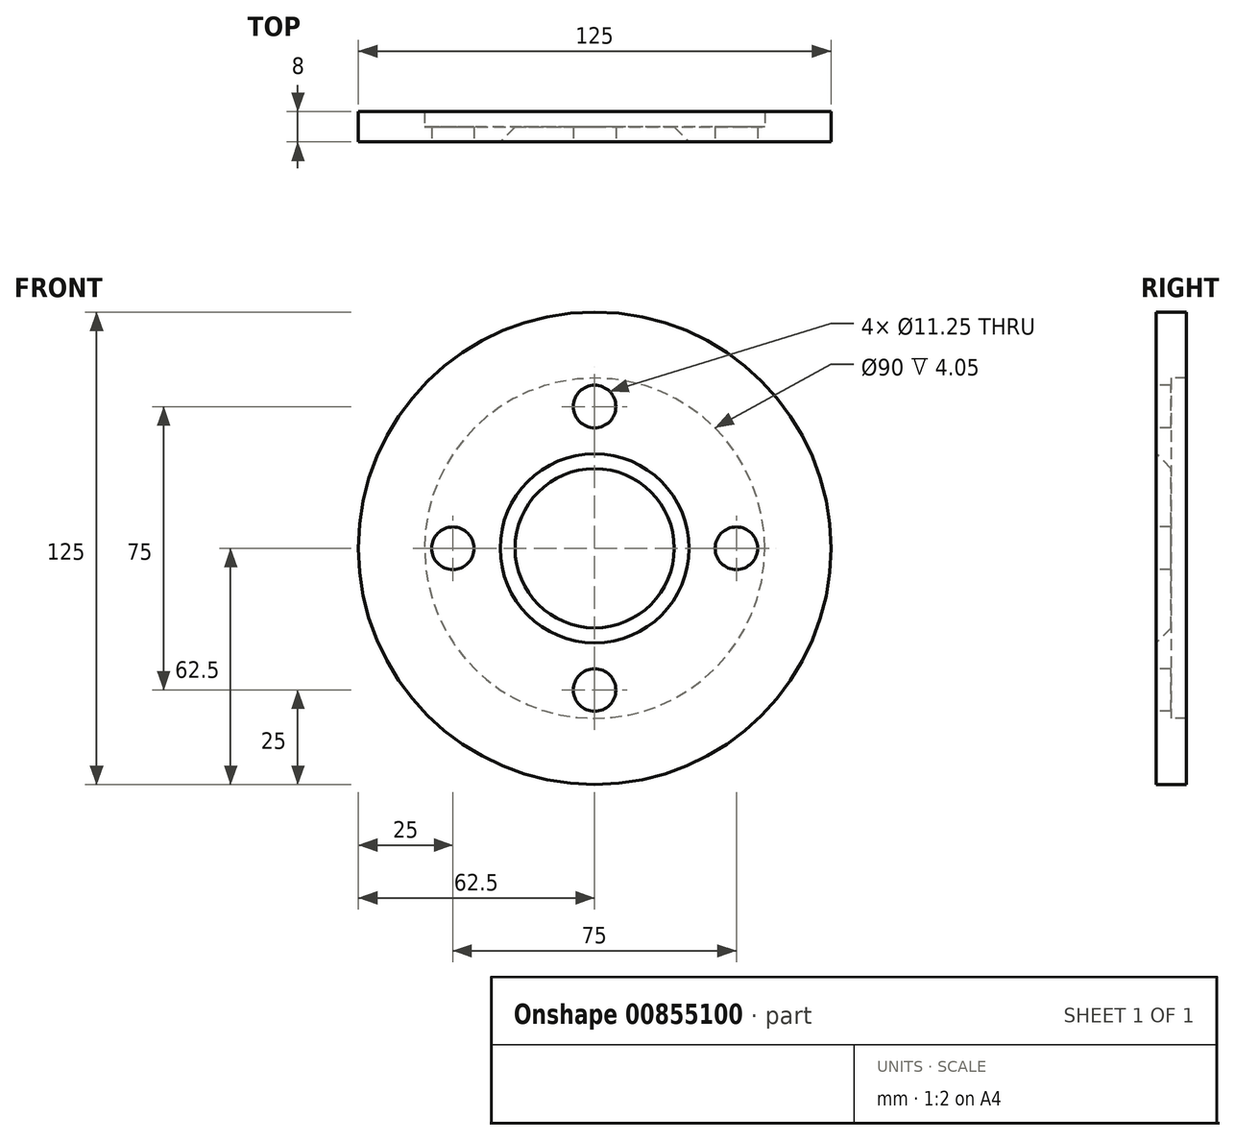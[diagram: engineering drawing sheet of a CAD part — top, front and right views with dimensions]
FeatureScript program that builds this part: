
annotation { "Feature Type Name" : "Feature", "Feature Type Description" : "" }
export const myFeature = defineFeature(function(context is Context, id is Id, definition is map)
    precondition{}
    {
        {
            var Q0;
            Q0=qCreatedBy(makeId("Front.planeOp"),FACE);
            var sketch = newSketch(context, id + "F0", { "sketchPlane" : qUnion([Q0])});
            skCircle(sketch, "E0", {"center": v(0, 0) * mm, "radius": 62.5 * mm});
            skCircle(sketch, "E1", {"center": v(0, 0) * mm, "radius": 37.5 * mm, "construction": true});
            skPoint(sketch, "E2", {"position": v(0, 37.5) * mm});
            skPoint(sketch, "E3", {"position": v(37.5, 0) * mm});
            skPoint(sketch, "E4.MirrorP", {"position": v(0, -37.5) * mm});
            skPoint(sketch, "E5.MirrorP", {"position": v(-37.5, 0) * mm});
            skCircle(sketch, "E6", {"center": v(0, 0) * mm, "radius": 45 * mm, "construction": true});
            skSolve(sketch);
        }
        {
            var Q0;
            Q0=makeQuery(id+"F0.imprint","IMPRINT",FACE,{"disambiguationData":[TD([[makeQuery(id+"F0.imprint","IMPRINT",EDGE,{"derivedFrom":sQuery(id+"F0.wireOp",EDGE,"E0")}),1.0]])]});
            extrude(context, id + "F1", {"entities" : qUnion([Q0]), "oppositeDirection" : true, "depth" : 3.95 * mm, "offsetDistance" : 25 * mm});
        }
        {
            var Q0;
            Q0=makeQuery(id+"F1.opExtrude","CAP_FACE",FACE,{"disambiguationData":[OSD([sQuery(id+"F0.wireOp",EDGE,"E0")])],"isStart":false});
            var sketch = newSketch(context, id + "F2", { "sketchPlane" : qUnion([Q0])});
            skCircle(sketch, "E7.0", {"center": v(0, 0) * mm, "radius": 45 * mm});
            skSolve(sketch);
        }
        {
            var Q0;
            Q0=makeQuery(id+"F2.imprint","IMPRINT",FACE,{"disambiguationData":[TD([[makeQuery(id+"F2.imprint","IMPRINT",EDGE,{"derivedFrom":sQuery(id+"F2.wireOp",EDGE,"E7.0")}),-1.0]])]});
            extrude(context, id + "F3", {"entities" : qUnion([Q0]), "operationType" : NewBodyOperationType.ADD, "depth" : 4.05 * mm, "offsetDistance" : 25 * mm});
        }
        {
            var Q0;
            Q0=qCreatedBy(makeId("Top.planeOp"),FACE);
            var sketch = newSketch(context, id + "F4", { "sketchPlane" : qUnion([Q0])});
            skLineSegment(sketch, "E8", {"start": v(0, 0) * mm, "end": v(0, 8) * mm});
            skLineSegment(sketch, "E9", {"start": v(0, 8) * mm, "end": v(18, 8) * mm});
            skLineSegment(sketch, "E10", {"start": v(18, 8) * mm, "end": v(18, 7) * mm});
            skLineSegment(sketch, "E11", {"start": v(18, 7) * mm, "end": v(25, 0) * mm});
            skLineSegment(sketch, "E12", {"start": v(25, 0) * mm, "end": v(0, 0) * mm});
            skSolve(sketch);
        }
        {
            var Q0;
            Q0=makeQuery(id+"F4.imprint","IMPRINT",FACE,{"disambiguationData":[TD([[makeQuery(id+"F4.imprint","IMPRINT",EDGE,{"derivedFrom":sQuery(id+"F4.wireOp",EDGE,"E8")}),-1.0]])]});
            var Q1;
            Q1=sQuery(id+"F4.wireOp",EDGE,"E8");
            revolve(context, id + "F5", {"operationType" : NewBodyOperationType.REMOVE, "surfaceOperationType" : NewSurfaceOperationType.NEW, "entities" : qUnion([Q0]), "axis" : qUnion([Q1]), "revolveType" : RevolveType.FULL, "oppositeDirection" : true});
        }
        {
            var Q0;
            Q0=sQuery(id+"F0.wireOp",VERTEX,"E3");
            var Q1;
            Q1=sQuery(id+"F0.wireOp",VERTEX,"E4.MirrorP");
            var Q2;
            Q2=sQuery(id+"F0.wireOp",VERTEX,"E5.MirrorP");
            var Q3;
            Q3=sQuery(id+"F0.wireOp",VERTEX,"E2");
            var Q4;
            Q4=makeQuery(id+"F1.opExtrude","SWEPT_BODY",BODY,{"disambiguationData":[OSD([sQuery(id+"F0.wireOp",EDGE,"E0")])]});
            hole(context, id + "F6", {"style" : HoleStyle.C_BORE, "endStyle" : HoleEndStyle.BLIND, "standardTappedOrClearance" : lookupTablePath({ "standard" : "ISO", "engagement" : "75%", "pitch" : "1 mm", "size" : "M6", "type" : "Tapped" }), "standardBlindInLast" : lookupTablePath({ "standard" : "ISO", "engagement" : "75%", "pitch" : "1 mm", "size" : "M6", "type" : "Tapped" }), "holeDiameter" : 5 * mm, "cBoreDiameter" : 11.25 * mm, "cBoreDepth" : 6 * mm, "majorDiameter" : 6 * mm, "showTappedDepth" : true, "holeDepth" : 24.25 * mm, "tappedDepth" : 21.25 * mm, "tapClearance" : 3, "locations" : qUnion([Q0, Q1, Q2, Q3]), "scope" : qUnion([Q4])});
        }
    });
